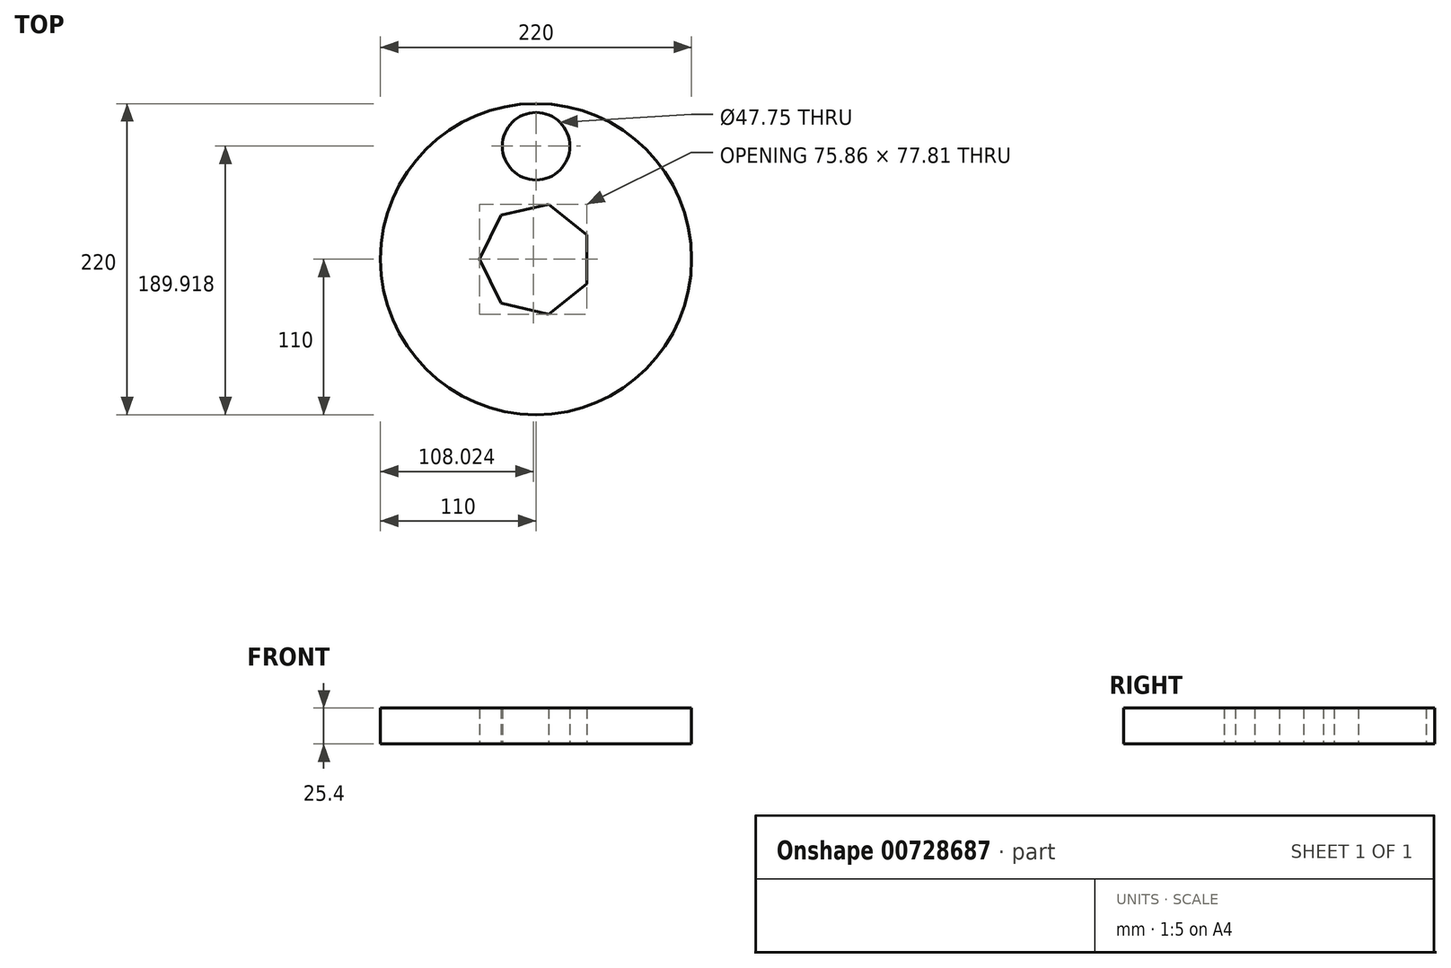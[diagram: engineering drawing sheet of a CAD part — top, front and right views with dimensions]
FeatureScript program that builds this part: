
annotation { "Feature Type Name" : "Feature", "Feature Type Description" : "" }
export const myFeature = defineFeature(function(context is Context, id is Id, definition is map)
    precondition{}
    {
        {
            var Q0;
            Q0=qCreatedBy(makeId("Top.planeOp"),FACE);
            var sketch = newSketch(context, id + "F0", { "sketchPlane" : qUnion([Q0])});
            skCircle(sketch, "E0", {"center": v(0, 0) * mm, "radius": 110 * mm});
            skCircle(sketch, "E1", {"center": v(0, 79.92) * mm, "radius": 23.87 * mm});
            skCircle(sketch, "E2.cCircle", {"center": v(0, 0) * mm, "radius": 35.95 * mm, "construction": true});
            skLineSegment(sketch, "E2.0", {"start": v(35.95, 17.31) * mm, "end": v(35.95, -17.31) * mm});
            skLineSegment(sketch, "E2.1", {"start": v(35.95, -17.31) * mm, "end": v(8.88, -38.9) * mm});
            skLineSegment(sketch, "E2.2", {"start": v(8.88, -38.9) * mm, "end": v(-24.88, -31.2) * mm});
            skLineSegment(sketch, "E2.3", {"start": v(-24.88, -31.2) * mm, "end": v(-39.9, 0) * mm});
            skLineSegment(sketch, "E2.4", {"start": v(-39.9, 0) * mm, "end": v(-24.88, 31.2) * mm});
            skLineSegment(sketch, "E2.5", {"start": v(-24.88, 31.2) * mm, "end": v(8.88, 38.9) * mm});
            skLineSegment(sketch, "E2.6", {"start": v(8.88, 38.9) * mm, "end": v(35.95, 17.31) * mm});
            skPoint(sketch, "E2.0.midPoint", {"position": v(35.95, 0) * mm});
            skSolve(sketch);
        }
        {
            var Q0;
            Q0=makeQuery(id+"F0.imprint","IMPRINT",FACE,{"disambiguationData":[TD([[makeQuery(id+"F0.imprint","IMPRINT",EDGE,{"derivedFrom":sQuery(id+"F0.wireOp",EDGE,"E0")}),1.0]])]});
            extrude(context, id + "F1", {"entities" : qUnion([Q0]), "depth" : 25.4 * mm, "offsetDistance" : 25.4 * mm});
        }
    });
